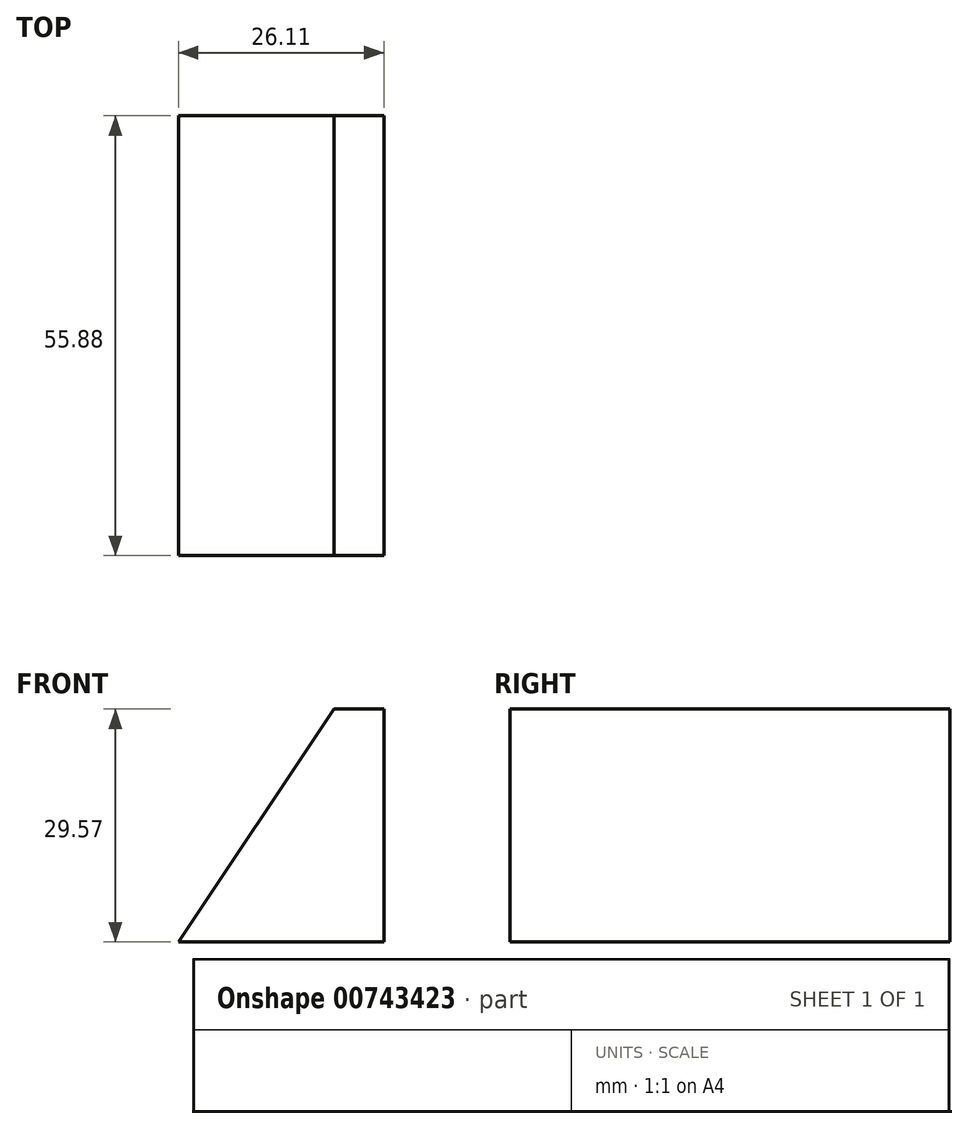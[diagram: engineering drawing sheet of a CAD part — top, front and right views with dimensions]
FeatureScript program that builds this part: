
annotation { "Feature Type Name" : "Feature", "Feature Type Description" : "" }
export const myFeature = defineFeature(function(context is Context, id is Id, definition is map)
    precondition{}
    {
        {
            var Q0;
            Q0=qCreatedBy(makeId("Front.planeOp"),FACE);
            var sketch = newSketch(context, id + "F0", { "sketchPlane" : qUnion([Q0])});
            skLineSegment(sketch, "E0", {"start": v(0, 0) * mm, "end": v(-26.1, 0) * mm});
            skLineSegment(sketch, "E1", {"start": v(-26.1, 0) * mm, "end": v(-6.35, 29.57) * mm});
            skLineSegment(sketch, "E2", {"start": v(-6.35, 29.57) * mm, "end": v(0, 29.57) * mm});
            skLineSegment(sketch, "E3", {"start": v(0, 29.57) * mm, "end": v(0, 0) * mm});
            skSolve(sketch);
        }
        {
            var Q0;
            Q0 = qSketchRegion(id + "F5JcY1JFAFa2rGU", true);
            var Q1;
            Q1 = qSketchRegion(id + "F0", true);
            extrude(context, id + "F1", {"entities" : qUnion([Q0, Q1]), "depth" : 55.88 * mm, "offsetDistance" : 25.4 * mm});
        }
    });
